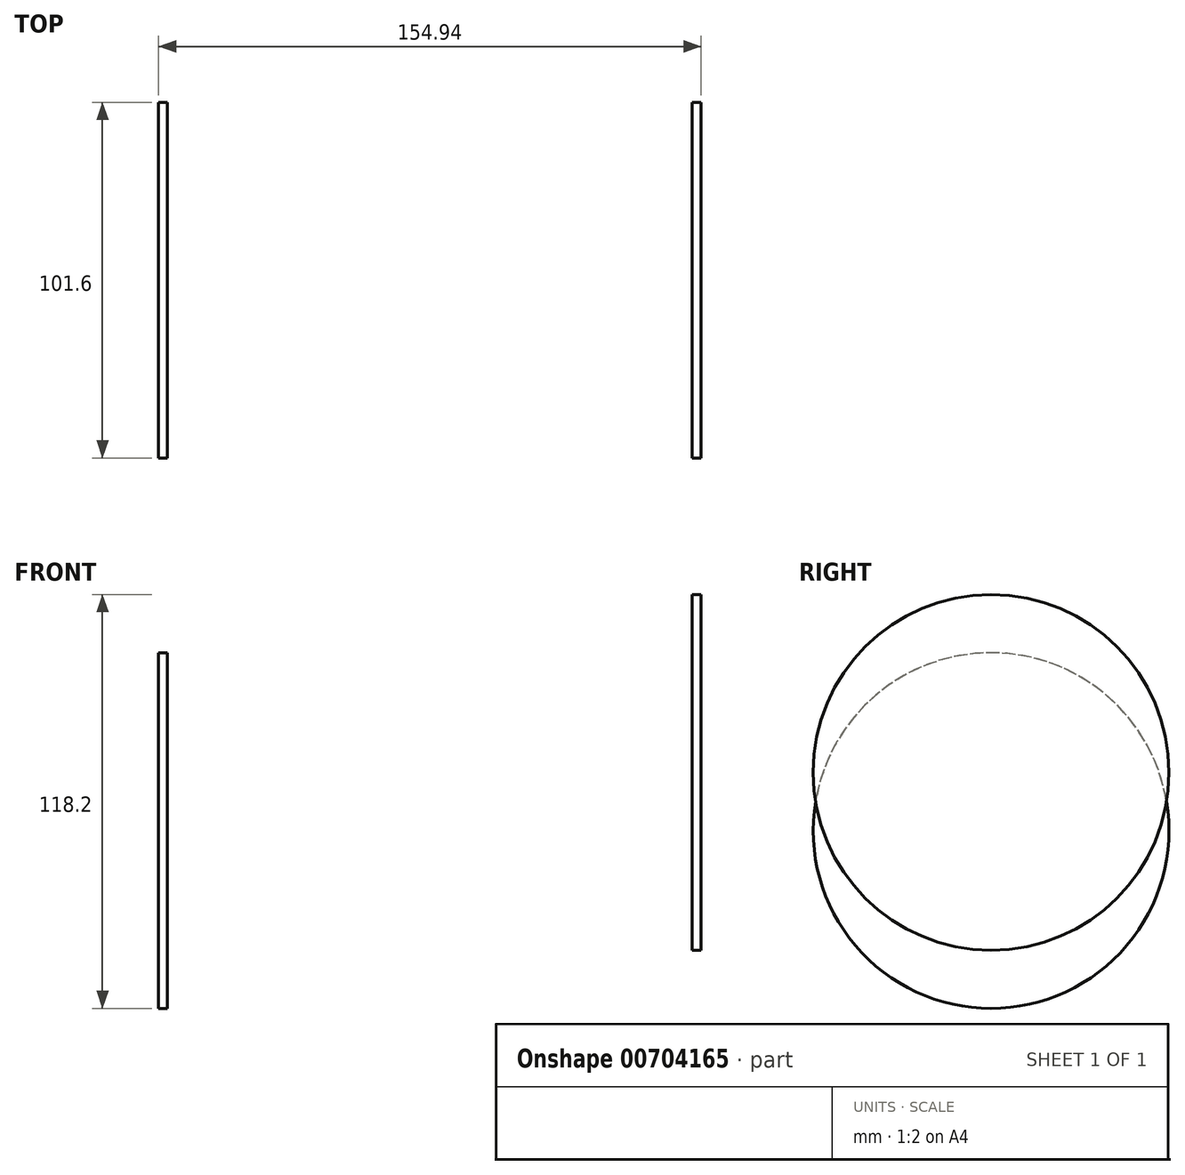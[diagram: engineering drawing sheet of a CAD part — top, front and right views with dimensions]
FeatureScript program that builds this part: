
annotation { "Feature Type Name" : "Feature", "Feature Type Description" : "" }
export const myFeature = defineFeature(function(context is Context, id is Id, definition is map)
    precondition{}
    {
        {
            var Q0;
            Q0=qCreatedBy(makeId("Right.planeOp"),FACE);
            var sketch = newSketch(context, id + "F0", { "sketchPlane" : qUnion([Q0])});
            skCircle(sketch, "E0", {"center": v(0, 0) * mm, "radius": 50.8 * mm});
            skSolve(sketch);
        }
        {
            var Q0;
            Q0=makeQuery(id+"F0.imprint","IMPRINT",FACE,{"disambiguationData":[TD([[makeQuery(id+"F0.imprint","IMPRINT",EDGE,{"derivedFrom":sQuery(id+"F0.wireOp",EDGE,"E0")}),1.0]])]});
            cPlane(context, id + "F1", {"entities" : qUnion([Q0]), "cplaneType" : CPlaneType.OFFSET, "offset" : 76.2 * mm, "oppositeDirection" : true, "width" : 152.4 * mm, "height" : 152.4 * mm});
        }
        {
            var Q0;
            Q0=makeQuery(id+"F0.imprint","IMPRINT",FACE,{"disambiguationData":[TD([[makeQuery(id+"F0.imprint","IMPRINT",EDGE,{"derivedFrom":sQuery(id+"F0.wireOp",EDGE,"E0")}),1.0]])]});
            cPlane(context, id + "F2", {"entities" : qUnion([Q0]), "cplaneType" : CPlaneType.OFFSET, "offset" : 76.2 * mm, "width" : 152.4 * mm, "height" : 152.4 * mm});
        }
        {
            var Q0;
            Q0=qCreatedBy(id+"F1.planeOp",FACE);
            var sketch = newSketch(context, id + "F3", { "sketchPlane" : qUnion([Q0])});
            skCircle(sketch, "E1", {"center": v(0, -16.6) * mm, "radius": 50.8 * mm});
            skSolve(sketch);
        }
        {
            var Q0;
            Q0=qCreatedBy(id+"F2.planeOp",FACE);
            var sketch = newSketch(context, id + "F4", { "sketchPlane" : qUnion([Q0])});
            skCircle(sketch, "E2", {"center": v(0, 0) * mm, "radius": 50.8 * mm});
            skSolve(sketch);
        }
        {
            var Q0;
            Q0=makeQuery(id+"F4.imprint","IMPRINT",FACE,{"disambiguationData":[TD([[makeQuery(id+"F4.imprint","IMPRINT",EDGE,{"derivedFrom":sQuery(id+"F4.wireOp",EDGE,"E2")}),1.0]])]});
            var Q1;
            Q1=makeQuery(id+"F3.imprint","IMPRINT",FACE,{"disambiguationData":[TD([[makeQuery(id+"F3.imprint","IMPRINT",EDGE,{"derivedFrom":sQuery(id+"F3.wireOp",EDGE,"E1")}),1.0]])]});
            extrude(context, id + "F5", {"entities" : qUnion([Q0, Q1]), "depth" : 2.54 * mm, "offsetDistance" : 25.4 * mm});
        }
    });
